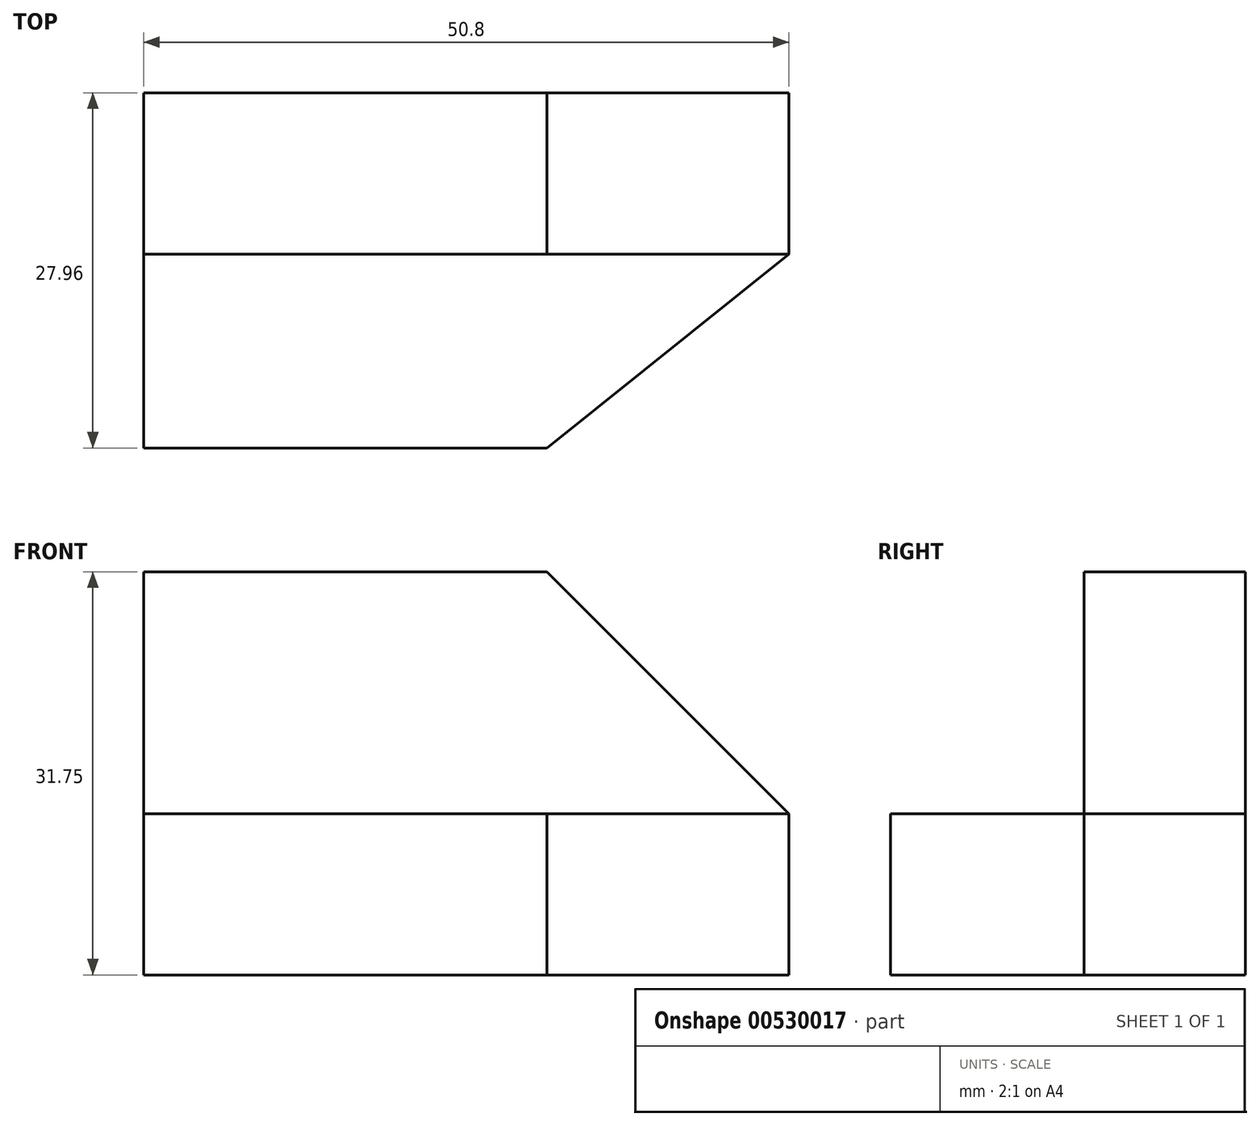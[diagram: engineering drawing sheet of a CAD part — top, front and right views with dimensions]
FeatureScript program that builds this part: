
annotation { "Feature Type Name" : "Feature", "Feature Type Description" : "" }
export const myFeature = defineFeature(function(context is Context, id is Id, definition is map)
    precondition{}
    {
        {
            var Q0;
            Q0=qCreatedBy(makeId("Right.planeOp"),FACE);
            var sketch = newSketch(context, id + "F0", { "sketchPlane" : qUnion([Q0])});
            skLineSegment(sketch, "E0", {"start": v(-24.72, 47.83) * mm, "end": v(-24.72, 16.08) * mm});
            skLineSegment(sketch, "E1", {"start": v(-24.72, 16.08) * mm, "end": v(-52.68, 16.08) * mm});
            skLineSegment(sketch, "E2", {"start": v(-52.68, 16.08) * mm, "end": v(-52.68, 28.78) * mm});
            skLineSegment(sketch, "E3", {"start": v(-52.68, 28.78) * mm, "end": v(-37.42, 28.78) * mm});
            skLineSegment(sketch, "E4", {"start": v(-37.42, 28.78) * mm, "end": v(-37.42, 47.83) * mm});
            skLineSegment(sketch, "E5", {"start": v(-37.42, 47.83) * mm, "end": v(-24.72, 47.83) * mm});
            skSolve(sketch);
        }
        {
            var Q0;
            Q0=makeQuery(id+"F0.imprint","IMPRINT",FACE,{"disambiguationData":[TD([[makeQuery(id+"F0.imprint","IMPRINT",EDGE,{"derivedFrom":sQuery(id+"F0.wireOp",EDGE,"E0")}),-1.0]])]});
            extrude(context, id + "F1", {"entities" : qUnion([Q0]), "depth" : 50.8 * mm, "offsetDistance" : 25.4 * mm});
        }
        {
            var Q0;
            Q0=makeQuery(id+"F1.opExtrude","SWEPT_FACE",FACE,{"disambiguationData":[OSD([sQuery(id+"F0.wireOp",EDGE,"E4")])]});
            var sketch = newSketch(context, id + "F2", { "sketchPlane" : qUnion([Q0])});
            skLineSegment(sketch, "E6", {"start": v(50.8, 28.78) * mm, "end": v(31.75, 47.83) * mm});
            skLineSegment(sketch, "E7", {"start": v(31.75, 47.83) * mm, "end": v(50.8, 47.83) * mm});
            skLineSegment(sketch, "E8", {"start": v(50.8, 47.83) * mm, "end": v(50.8, 28.78) * mm});
            skSolve(sketch);
        }
        {
            var Q0;
            Q0=makeQuery(id+"F2.imprint","IMPRINT",FACE,{"disambiguationData":[TD([[makeQuery(id+"F2.imprint","IMPRINT",EDGE,{"derivedFrom":sQuery(id+"F2.wireOp",EDGE,"E6")}),-1.0]])]});
            extrude(context, id + "F3", {"entities" : qUnion([Q0]), "operationType" : NewBodyOperationType.REMOVE, "endBound" : BoundingType.THROUGH_ALL, "oppositeDirection" : true, "depth" : 25.4 * mm, "offsetDistance" : 25.4 * mm});
        }
        {
            var Q0;
            Q0=makeQuery(id+"F1.opExtrude","SWEPT_FACE",FACE,{"disambiguationData":[OSD([sQuery(id+"F0.wireOp",EDGE,"E3")])]});
            var sketch = newSketch(context, id + "F4", { "sketchPlane" : qUnion([Q0])});
            skLineSegment(sketch, "E9", {"start": v(50.8, -37.42) * mm, "end": v(31.75, -52.68) * mm});
            skLineSegment(sketch, "E10", {"start": v(31.75, -52.68) * mm, "end": v(50.8, -52.68) * mm});
            skLineSegment(sketch, "E11", {"start": v(50.8, -52.68) * mm, "end": v(50.8, -37.42) * mm});
            skLineSegment(sketch, "E12", {"start": v(-26.87, -23.11) * mm, "end": v(-28.65, -14.22) * mm});
            skSolve(sketch);
        }
        {
            var Q0;
            Q0=makeQuery(id+"F4.imprint","IMPRINT",FACE,{"disambiguationData":[TD([[makeQuery(id+"F4.imprint","IMPRINT",EDGE,{"derivedFrom":sQuery(id+"F4.wireOp",EDGE,"E9")}),1.0]])]});
            extrude(context, id + "F5", {"entities" : qUnion([Q0]), "operationType" : NewBodyOperationType.REMOVE, "endBound" : BoundingType.THROUGH_ALL, "oppositeDirection" : true, "depth" : 25.4 * mm, "offsetDistance" : 25.4 * mm});
        }
    });
